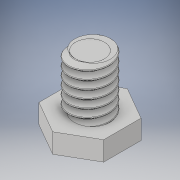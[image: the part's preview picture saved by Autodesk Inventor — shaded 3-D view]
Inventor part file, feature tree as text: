
AUTODESK INVENTOR PART (.ipt)
format: ipt  version: 2019 (Build 230136000, 136)  size: 634,368 bytes
history: native  units: in
note: dims shown in document units (in); Inventor stores cm internally (conversion verified against a paired STEP export)
features: sketch x5, extrude x2, revolve x2, thread x1, helix x1
ambient origin geometry x8: Origin, YZ Plane, XZ Plane, XY Plane, X Axis, Y Axis, Z Axis, Center Point
bodies: Solid1 (feature_tree), Solid2 (feature_tree)
feature tree (11):
  extrude  "Extrusion1"  Depth=0.315in TaperAngle=0.0deg
  extrude  "Extrusion2"  Depth=0.3937in TaperAngle=0.0deg
  thread  "Thread1"  [1 undecoded]
  revolve  "Revolution1"  [1 undecoded]
  revolve  "Revolution2"  [1 undecoded]
  helix  "Coil2"  [1 undecoded]
  sketch  "Sketch1"  dims[d0=0.25in d1=0.315in d2=0.0in]
  sketch  "Sketch2"  dims[d3=0.3937in d4=0.1181in d5=0.0in d16=0.3937in d17=0.0in]
  sketch  "Sketch4"  dims[d18=0.3779in d19=0.008in d20=0.008in d23=0.05in]
  sketch  "Sketch5"  dims[d25=0.3779in d27=0.0in d28=0.0in]
  sketch  "Sketch6"  dims[d29=0.05in d30=0.415in d31=0.3937in d32=0.0in d33=0.0in d34=0.0in d35=0.0in d36=0.0in]
note: 4 required parameter values undecoded (feature->parameter linkage not recoverable at this tier; creation-order binding heuristic only, values carry confidence <= 0.55)